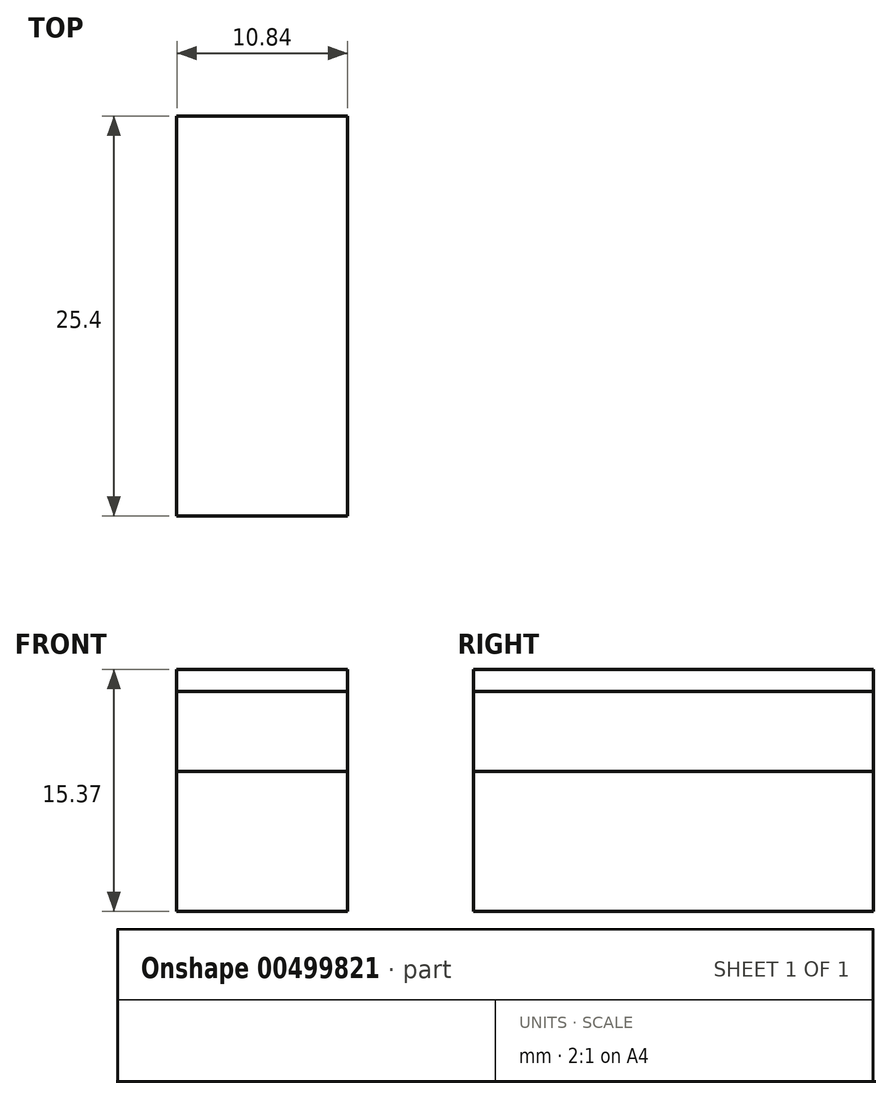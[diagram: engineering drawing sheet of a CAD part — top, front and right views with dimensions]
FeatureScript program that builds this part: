
annotation { "Feature Type Name" : "Feature", "Feature Type Description" : "" }
export const myFeature = defineFeature(function(context is Context, id is Id, definition is map)
    precondition{}
    {
        {
            var Q0;
            Q0=qCreatedBy(makeId("Front.planeOp"),FACE);
            var sketch = newSketch(context, id + "F0", { "sketchPlane" : qUnion([Q0])});
            skLineSegment(sketch, "E0.bottom", {"start": v(-5.42, 0) * mm, "end": v(5.42, 0) * mm});
            skLineSegment(sketch, "E0.top", {"start": v(-5.42, -1.4) * mm, "end": v(5.42, -1.4) * mm});
            skLineSegment(sketch, "E0.left", {"start": v(-5.42, 0) * mm, "end": v(-5.42, -1.4) * mm});
            skLineSegment(sketch, "E0.right", {"start": v(5.42, 0) * mm, "end": v(5.42, -1.4) * mm});
            skPoint(sketch, "E1", {"position": v(0, -0.7) * mm});
            skSolve(sketch);
        }
        {
            var Q0;
            Q0 = qSketchRegion(id + "F0", true);
            extrude(context, id + "F1", {"entities" : qUnion([Q0]), "oppositeDirection" : true, "depth" : 25.4 * mm});
        }
        {
            var Q0;
            Q0=qCreatedBy(makeId("Front.planeOp"),FACE);
            var sketch = newSketch(context, id + "F2", { "sketchPlane" : qUnion([Q0])});
            skLineSegment(sketch, "E2.bottom", {"start": v(-5.42, -1.4) * mm, "end": v(5.42, -1.4) * mm});
            skLineSegment(sketch, "E2.top", {"start": v(-5.42, -6.48) * mm, "end": v(5.42, -6.48) * mm});
            skLineSegment(sketch, "E2.left", {"start": v(-5.42, -1.4) * mm, "end": v(-5.42, -6.48) * mm});
            skLineSegment(sketch, "E2.right", {"start": v(5.42, -1.4) * mm, "end": v(5.42, -6.48) * mm});
            skPoint(sketch, "E3", {"position": v(0, -3.94) * mm});
            skSolve(sketch);
        }
        {
            var Q0;
            Q0 = qSketchRegion(id + "F2", true);
            extrude(context, id + "F3", {"entities" : qUnion([Q0]), "oppositeDirection" : true, "depth" : 25.4 * mm});
        }
        {
            var Q0;
            Q0=qCreatedBy(makeId("Front.planeOp"),FACE);
            var sketch = newSketch(context, id + "F4", { "sketchPlane" : qUnion([Q0])});
            skLineSegment(sketch, "E4.bottom", {"start": v(-5.42, -6.48) * mm, "end": v(5.42, -6.48) * mm});
            skLineSegment(sketch, "E4.top", {"start": v(-5.42, -15.37) * mm, "end": v(5.42, -15.37) * mm});
            skLineSegment(sketch, "E4.left", {"start": v(-5.42, -6.48) * mm, "end": v(-5.42, -15.37) * mm});
            skLineSegment(sketch, "E4.right", {"start": v(5.42, -6.48) * mm, "end": v(5.42, -15.37) * mm});
            skPoint(sketch, "E5", {"position": v(0, -10.92) * mm});
            skSolve(sketch);
        }
        {
            var Q0;
            Q0 = qSketchRegion(id + "F4", true);
            extrude(context, id + "F5", {"entities" : qUnion([Q0]), "oppositeDirection" : true, "offsetDistance" : 25.4 * mm, "depth" : 25.4 * mm});
        }
    });
